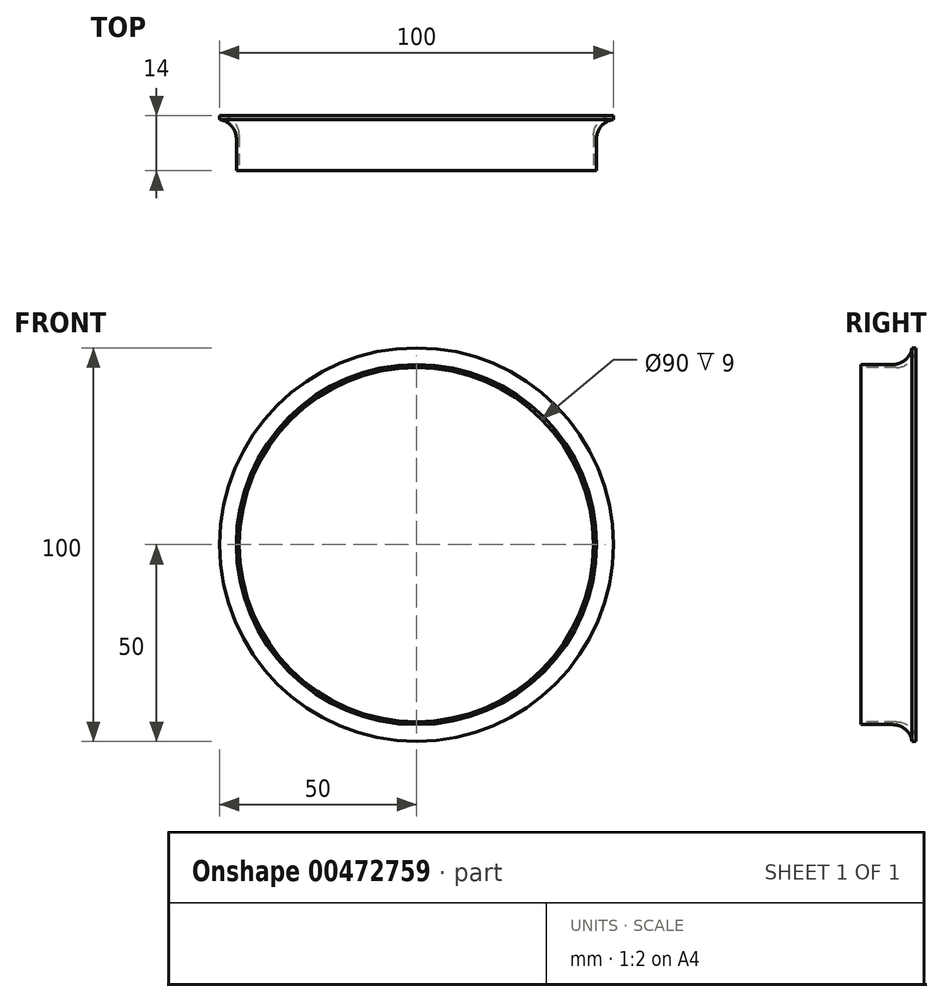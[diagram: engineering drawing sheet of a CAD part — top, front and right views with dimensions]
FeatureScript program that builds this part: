
annotation { "Feature Type Name" : "Feature", "Feature Type Description" : "" }
export const myFeature = defineFeature(function(context is Context, id is Id, definition is map)
    precondition{}
    {
        {
            var Q0;
            Q0=qCreatedBy(makeId("Front.planeOp"),FACE);
            var sketch = newSketch(context, id + "F0", { "sketchPlane" : qUnion([Q0])});
            skCircle(sketch, "E0", {"center": v(0, 0) * mm, "radius": 50 * mm});
            skCircle(sketch, "E1", {"center": v(0, 0) * mm, "radius": 45 * mm});
            skSolve(sketch);
        }
        {
            var Q0;
            Q0=makeQuery(id+"F0.imprint","IMPRINT",FACE,{"disambiguationData":[TD([[makeQuery(id+"F0.imprint","IMPRINT",EDGE,{"derivedFrom":sQuery(id+"F0.wireOp",EDGE,"E0")}),1.0]])]});
            extrude(context, id + "F1", {"entities" : qUnion([Q0]), "depth" : 1 * mm});
        }
        {
            var Q0;
            Q0=qCreatedBy(makeId("Front.planeOp"),FACE);
            var sketch = newSketch(context, id + "F2", { "sketchPlane" : qUnion([Q0])});
            skCircle(sketch, "E2", {"center": v(0, 0) * mm, "radius": 45.75 * mm});
            skSolve(sketch);
        }
        {
            var Q0;
            Q0=makeQuery(id+"F2.imprint","IMPRINT",FACE,{"disambiguationData":[TD([[makeQuery(id+"F2.imprint","IMPRINT",EDGE,{"derivedFrom":sQuery(id+"F2.wireOp",EDGE,"E2")}),1.0]])]});
            extrude(context, id + "F3", {"entities" : qUnion([Q0]), "operationType" : NewBodyOperationType.ADD, "depth" : 14 * mm});
        }
        {
            var Q0;
            Q0=makeQuery(id+"F3.boolean.opBoolean","INTERSECT",EDGE,{"derivedFrom":[makeQuery(id+"F1.opExtrude","CAP_FACE",FACE,{"disambiguationData":[OSD([sQuery(id+"F0.wireOp",EDGE,"E0"),sQuery(id+"F0.wireOp",EDGE,"E1")])],"isStart":false}),makeQuery(id+"F3.opExtrude","SWEPT_FACE",FACE,{"disambiguationData":[OSD([sQuery(id+"F2.wireOp",EDGE,"E2")])]})]});
            fillet(context, id + "F4", {"entities" : qUnion([Q0]), "radius" : 5 * mm, "tangentPropagation" : true, "allowEdgeOverflow" : false});
        }
        {
            var Q0;
            Q0=makeQuery(id+"F3.opExtrude","CAP_FACE",FACE,{"disambiguationData":[OSD([sQuery(id+"F2.wireOp",EDGE,"E2")])],"isStart":false});
            var sketch = newSketch(context, id + "F5", { "sketchPlane" : qUnion([Q0])});
            skCircle(sketch, "E3", {"center": v(0, 0) * mm, "radius": 45 * mm});
            skSolve(sketch);
        }
        {
            var Q0;
            Q0=makeQuery(id+"F5.imprint","IMPRINT",FACE,{"disambiguationData":[TD([[makeQuery(id+"F5.imprint","IMPRINT",EDGE,{"derivedFrom":sQuery(id+"F5.wireOp",EDGE,"E3")}),1.0]])]});
            extrude(context, id + "F6", {"entities" : qUnion([Q0]), "operationType" : NewBodyOperationType.REMOVE, "oppositeDirection" : true, "depth" : 17 * mm});
        }
        {
            var Q0;
            Q0=makeQuery(id+"F6.boolean.opBoolean","INTERSECT",EDGE,{"derivedFrom":[makeQuery(id+"F3.boolean.opBoolean","MERGE",FACE,{"derivedFrom":[makeQuery(id+"F1.opExtrude","CAP_FACE",FACE,{"disambiguationData":[OSD([sQuery(id+"F0.wireOp",EDGE,"E0"),sQuery(id+"F0.wireOp",EDGE,"E1")])],"isStart":true}),makeQuery(id+"F3.opExtrude","CAP_FACE",FACE,{"disambiguationData":[OSD([sQuery(id+"F2.wireOp",EDGE,"E2")])],"isStart":true})]}),makeQuery(id+"F6.opExtrude","SWEPT_FACE",FACE,{"disambiguationData":[OSD([sQuery(id+"F5.wireOp",EDGE,"E3")])]})]});
            fillet(context, id + "F7", {"entities" : qUnion([Q0]), "radius" : 5 * mm, "tangentPropagation" : true, "allowEdgeOverflow" : false});
        }
    });
